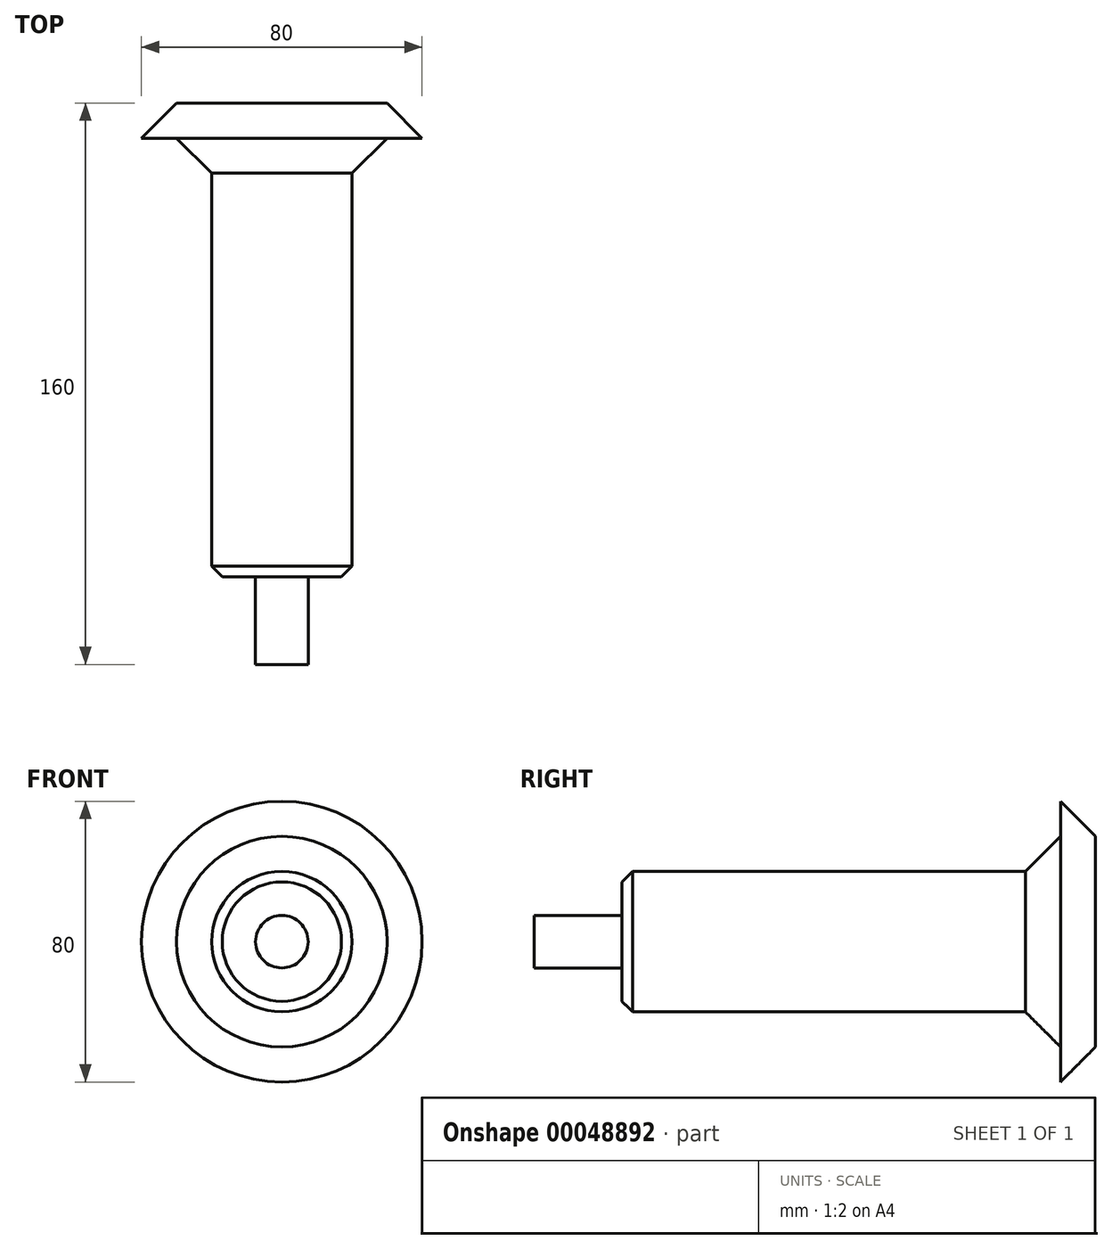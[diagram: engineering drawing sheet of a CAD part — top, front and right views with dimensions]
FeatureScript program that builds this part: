
annotation { "Feature Type Name" : "Feature", "Feature Type Description" : "" }
export const myFeature = defineFeature(function(context is Context, id is Id, definition is map)
    precondition{}
    {
        {
            var Q0;
            Q0=qCreatedBy(makeId("Right.planeOp"),FACE);
            var sketch = newSketch(context, id + "F0", { "sketchPlane" : qUnion([Q0])});
            skLineSegment(sketch, "E0", {"start": v(-160, 0) * mm, "end": v(0, 0) * mm, "construction": true});
            skLineSegment(sketch, "E1", {"start": v(-160, 0) * mm, "end": v(-10, 0) * mm, "construction": true});
            skLineSegment(sketch, "E2", {"start": v(-10, 30) * mm, "end": v(-10, 40) * mm});
            skLineSegment(sketch, "E3", {"start": v(-10, 40) * mm, "end": v(0, 30) * mm});
            skLineSegment(sketch, "E4", {"start": v(0, 30) * mm, "end": v(0, 0) * mm});
            skLineSegment(sketch, "E5", {"start": v(-160, 0) * mm, "end": v(-135, 0) * mm, "construction": true});
            skLineSegment(sketch, "E6", {"start": v(-160, 0) * mm, "end": v(-160, 20) * mm, "construction": true});
            skLineSegment(sketch, "E7", {"start": v(-160, 20) * mm, "end": v(-10, 20) * mm, "construction": true});
            skLineSegment(sketch, "E8", {"start": v(-10, 30) * mm, "end": v(-20, 20) * mm});
            skLineSegment(sketch, "E9", {"start": v(-135, 7.5) * mm, "end": v(-135, 20) * mm, "construction": true});
            skLineSegment(sketch, "E10", {"start": v(-160, 0) * mm, "end": v(-160, 7.5) * mm});
            skLineSegment(sketch, "E11", {"start": v(-160, 7.5) * mm, "end": v(-135, 7.5) * mm});
            skLineSegment(sketch, "E12", {"start": v(-135, 17) * mm, "end": v(-132, 20) * mm});
            skLineSegment(sketch, "E13", {"start": v(-135, 7.5) * mm, "end": v(-135, 17) * mm});
            skLineSegment(sketch, "E14", {"start": v(-132, 20) * mm, "end": v(-20, 20) * mm});
            skLineSegment(sketch, "E15", {"start": v(-160, 0) * mm, "end": v(0, 0) * mm});
            skSolve(sketch);
        }
        {
            var Q0;
            Q0=makeQuery(id+"F0.imprint","IMPRINT",FACE,{"disambiguationData":[TD([[makeQuery(id+"F0.imprint","IMPRINT",EDGE,{"derivedFrom":sQuery(id+"F0.wireOp",EDGE,"E2")}),-1.0]])]});
            var Q1;
            Q1=sQuery(id+"F0.wireOp",EDGE,"E15");
            revolve(context, id + "F1", {"entities" : qUnion([Q0]), "axis" : qUnion([Q1]), "revolveType" : RevolveType.FULL});
        }
    });
